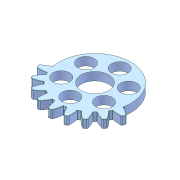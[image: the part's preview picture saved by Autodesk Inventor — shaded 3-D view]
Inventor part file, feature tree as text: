
AUTODESK INVENTOR PART (.ipt)
format: ipt  version: unknown  size: 1,448,960 bytes
history: native  units: mm (DEFAULTED — no unit token found)
features: sketch x6, extrude x5, fillet x4, other x1, pattern_circular x1
ambient origin geometry x8: Origin, YZ Plane, XZ Plane, XY Plane, X Axis, Y Axis, Z Axis, Center Point
feature tree (17):
  extrude  "Extrusion1"  Depth=6.0mm TaperAngle=0.0deg
  other  "Spur Gear"
  sketch  "Sketch9"  dims[d43=60.0mm d46=60.0mm d70=60.0mm d131=1.0mm]
  fillet  "Fillet2"  Radius=60.0mm
  fillet  "Fillet3"  [1 undecoded]
  extrude  "Extrusion24"  Depth=60.0mm
  fillet  "Fillet4"  Radius=60.0mm
  fillet  "Fillet5"  Radius=1.0mm
  extrude  "Extrusion25"  Depth=20.0mm
  extrude  "Extrusion26"  Depth=8.0mm
  extrude  "Extrusion27"  Depth=2.5mm
  pattern_circular  "Circular Pattern2"  [2 undecoded]
  sketch  "Sketch1"  dims[d0=66.0mm d1=6.0mm d2=0.0mm d16=60.0mm d41=0.0mm]
  sketch  "Sketch31"  dims[d136=1.0mm d137=20.0mm]
  sketch  "Sketch32"  dims[d138=5.0mm d139=8.0mm]
  sketch  "Sketch33"  dims[d140=4.0mm d141=2.5mm]
  sketch  "Sketch34"  dims[d142=10.0mm d143=0.0mm d144=0.2mm d145=0.2mm d146=13.962634mm d147=52.0mm d148=10.0mm d149=0.0mm d150=10.0mm d151=0.0mm d152=18.0mm d153=12.0mm d154=10.0mm d155=0.0mm d156=60.0mm d157=360.0deg]
note: 3 required parameter values undecoded (feature->parameter linkage not recoverable at this tier; creation-order binding heuristic only, values carry confidence <= 0.55)
